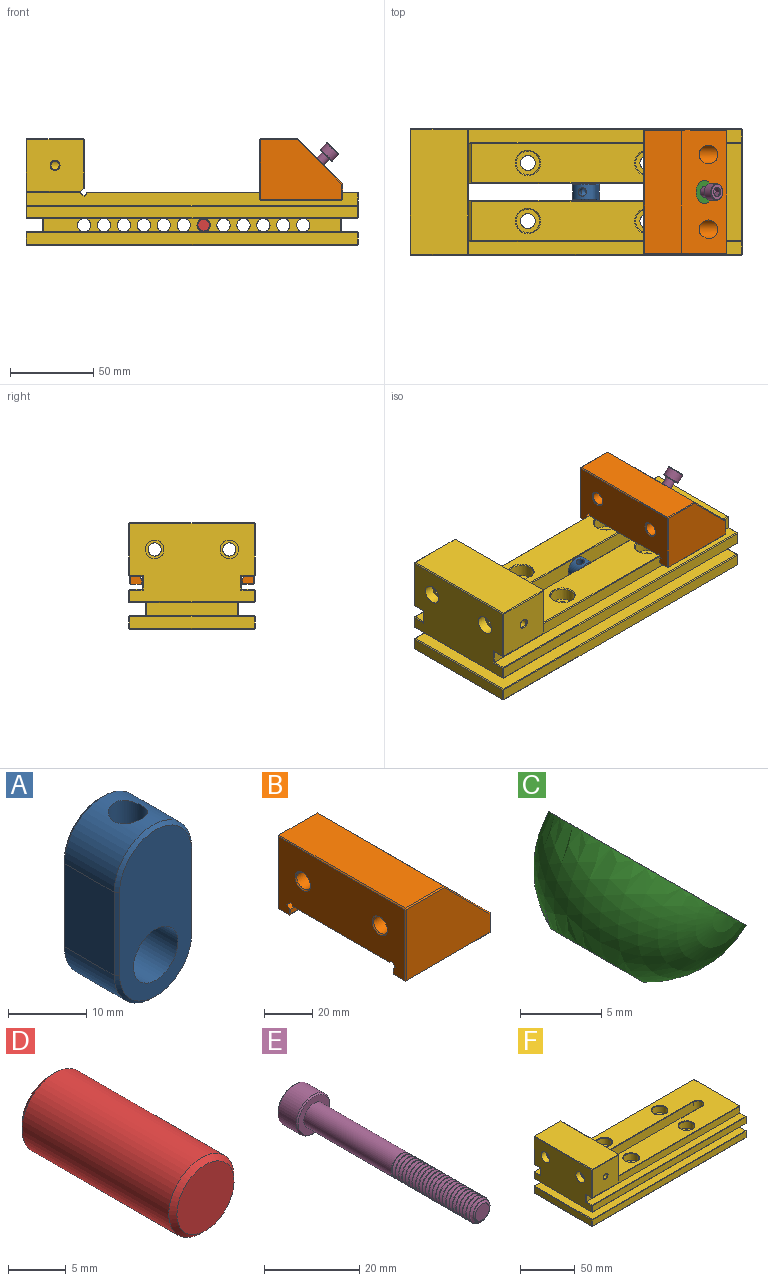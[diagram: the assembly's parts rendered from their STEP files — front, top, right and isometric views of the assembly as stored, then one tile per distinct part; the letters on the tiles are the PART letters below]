
ASSEMBLY  parts=6 mates=6
PART A: 17 faces, bbox 14x10x27 mm
  f0: cylinder r=7mm len=14mm, axis (0,1,0), area 178mm2, adj f1,f3,f7,f11,f15
  f1: plane 13x9mm, normal (-1,0,0), area 117mm2, adj f0,f2,f8,f12
  f2: cylinder r=7mm len=14mm, axis (0,1,0), area 197.9mm2, adj f1,f3,f10,f14
  f3: plane 13x9mm, normal (1,0,0), area 117mm2, adj f0,f2,f9,f13
  f4: cylinder r=4mm len=10mm, axis (0,1,0), area 251.3mm2, adj f5,f6
  f5: plane 26x13mm, normal (0,-1,0), area 251.5mm2, adj f4,f11,f12,f13,f14
  f6: plane 26x13mm, normal (0,1,0), area 251.5mm2, adj f4,f7,f8,f9,f10
  f7: cone r=7mm half-angle=45deg, axis (0,-1,0), area 15mm2, adj f0,f6,f8,f9
  f8: plane 13x0.5mm, normal (-0.71,0.71,0), area 9.2mm2, adj f1,f6,f7,f10
  f9: plane 13x0.5mm, normal (0.71,0.71,0), area 9.2mm2, adj f3,f6,f7,f10
  f10: cone r=7mm half-angle=45deg, axis (0,-1,0), area 15mm2, adj f2,f6,f8,f9
  f11: cone r=6.5mm half-angle=45deg, axis (0,1,0), area 15mm2, adj f0,f5,f12,f13
  f12: plane 13x0.5mm, normal (-0.71,-0.71,0), area 9.2mm2, adj f1,f5,f11,f14
  f13: plane 13x0.5mm, normal (0.71,-0.71,0), area 9.2mm2, adj f3,f5,f11,f14
  f14: cone r=6.5mm half-angle=45deg, axis (0,1,0), area 15mm2, adj f2,f5,f12,f13
  f15: cylinder r=2.5mm len=10.46mm, axis (0,0,1), area 160.7mm2, adj f0,f16
  f16: cone r=0mm half-angle=59deg, axis (0,0,1), area 22.9mm2, adj f15
PART B: 55 faces, bbox 50x75x42 mm
  f0: plane 55.76x49mm, normal (0,0,-1), area 2514.4mm2, adj f18,f23,f24,f51,f54
  f1: plane 74x9.5mm, normal (1,0,0), area 394.4mm2, adj f8,f9,f10,f21,f22,f23,f24,f25
  f2: plane 74x36.5mm, normal (-1,0,0), area 2228.8mm2, adj f3,f21,f22,f23,f24,f25,f26,f27
  f3: plane 49.5x6.5mm, normal (0,0,-1), area 321.7mm2, adj f2,f28,f29,f32
  f4: plane 49x36mm, normal (0,1,0), area 1407.4mm2, adj f31,f32,f33,f34,f35
  f5: plane 74x22.5mm, normal (0,0,1), area 1665mm2, adj f10,f35,f37,f38
  f6: plane 49x36mm, normal (0,-1,0), area 1407.4mm2, adj f38,f39,f41,f42,f43
  f7: plane 49x6.5mm, normal (0,0,-1), area 318.5mm2, adj f43,f46,f47,f48
  f8: plane 49.5x2.38mm, normal (0,1,0), area 117.7mm2, adj f1,f26,f48,f50
  f9: plane 49.5x2.38mm, normal (0,-1,0), area 117.7mm2, adj f1,f21,f27,f28
  f10: plane 74x27mm, normal (0.71,0,0.71), area 2390.5mm2, adj f1,f5,f11,f13,f16,f33,f39
  f11: cylinder r=5.62mm len=11.63mm, axis (1,0,0), area 212.1mm2, adj f10,f12
  f12: plane 11.25x11.25mm, normal (1,0,0), area 49.1mm2, adj f11,f19
  f13: cylinder r=5.62mm len=11.63mm, axis (1,0,0), area 212.1mm2, adj f10,f14
  f14: plane 11.25x11.25mm, normal (1,0,0), area 49.1mm2, adj f13,f20
  f15: cylinder r=4mm len=10.08mm, axis (0.71,0,0.71), area 157.2mm2, adj f16,f17
  f16: sphere r=7mm, area 252.7mm2, adj f10,f15
  f17: plane 14x9.9mm, normal (-0.71,0,-0.71), area 103.7mm2, adj f15,f18
  f18: cylinder r=7mm len=24.93mm, axis (0.71,0,0.71), area 622.9mm2, adj f0,f17
  f19: cylinder r=4mm len=32.5mm, axis (-1,0,0), area 816.8mm2, adj f12,f53
  f20: cylinder r=4mm len=32.5mm, axis (-1,0,0), area 816.8mm2, adj f14,f52
  f21: plane 50x1.77mm, normal (0,-0.71,0.71), area 124.8mm2, adj f1,f2,f9,f22,f27
  f22: plane 50x2.12mm, normal (0,-0.71,-0.71), area 150mm2, adj f1,f2,f21,f23
  f23: plane 50x1.77mm, normal (0,0.71,-0.71), area 124.6mm2, adj f0,f1,f2,f22,f51,f54
  f24: plane 50x1.77mm, normal (0,-0.71,-0.71), area 124.6mm2, adj f0,f1,f2,f25,f51,f54
  f25: plane 50x2.12mm, normal (0,0.71,-0.71), area 150mm2, adj f1,f2,f24,f26
  f26: plane 50x1.77mm, normal (0,0.71,0.71), area 124.8mm2, adj f1,f2,f8,f25,f50
  f27: plane 3.38x0.5mm, normal (-0.71,-0.71,0), area 2mm2, adj f2,f9,f21,f28
  f28: plane 50x0.5mm, normal (0,-0.71,-0.71), area 35mm2, adj f3,f9,f27,f29
  f29: plane 7x0.5mm, normal (0.71,0,-0.71), area 4.8mm2, adj f1,f3,f28,f30
  f30: plane 0.5x0.5mm, normal (0.58,0.58,-0.58), area 0.2mm2, adj f29,f31,f32
  f31: plane 9.5x0.5mm, normal (0.71,0.71,0), area 6.6mm2, adj f1,f4,f30,f33
  f32: plane 49.5x0.5mm, normal (0,0.71,-0.71), area 34.8mm2, adj f3,f4,f30,f34
  f33: plane 27.21x27.21mm, normal (0.5,0.71,0.5), area 26.9mm2, adj f4,f10,f31,f35
  f34: plane 36.5x0.5mm, normal (-0.71,0.71,0), area 25.6mm2, adj f2,f4,f32,f36
  f35: plane 22.5x0.5mm, normal (0,0.71,0.71), area 15.8mm2, adj f4,f5,f33,f36
  f36: plane 0.5x0.5mm, normal (-0.58,0.58,0.58), area 0.2mm2, adj f34,f35,f37
  f37: plane 74x0.5mm, normal (-0.71,0,0.71), area 52.3mm2, adj f2,f5,f36,f40
  f38: plane 22.5x0.5mm, normal (0,-0.71,0.71), area 15.8mm2, adj f5,f6,f39,f40
  f39: plane 27.21x27.21mm, normal (0.5,-0.71,0.5), area 26.9mm2, adj f6,f10,f38,f41
  f40: plane 0.5x0.5mm, normal (-0.58,-0.58,0.58), area 0.2mm2, adj f37,f38,f42
  f41: plane 9.5x0.5mm, normal (0.71,-0.71,0), area 6.6mm2, adj f1,f6,f39,f44
  f42: plane 36x0.5mm, normal (-0.71,-0.71,0), area 25.5mm2, adj f2,f6,f40,f45
  f43: plane 49x0.5mm, normal (0,-0.71,-0.71), area 34.6mm2, adj f6,f7,f44,f45
  f44: plane 0.5x0.5mm, normal (0.58,-0.58,-0.58), area 0.2mm2, adj f41,f43,f46
  f45: plane 0.5x0.5mm, normal (-0.58,-0.58,-0.58), area 0.2mm2, adj f42,f43,f47
  f46: plane 7x0.5mm, normal (0.71,0,-0.71), area 4.8mm2, adj f1,f7,f44,f48
  f47: plane 6.5x0.5mm, normal (-0.71,0,-0.71), area 4.6mm2, adj f2,f7,f45,f49
  f48: plane 49.5x0.5mm, normal (0,0.71,-0.71), area 34.8mm2, adj f7,f8,f46,f49
  f49: plane 0.5x0.5mm, normal (-0.58,0.58,-0.58), area 0.2mm2, adj f47,f48,f50
  f50: plane 2.88x0.5mm, normal (-0.71,0.71,0), area 1.9mm2, adj f2,f8,f26,f49
  f51: plane 56.76x0.5mm, normal (0.71,0,-0.71), area 39.8mm2, adj f0,f1,f23,f24
  f52: cone r=4mm half-angle=45deg, axis (-1,0,0), area 18.9mm2, adj f2,f20
  f53: cone r=4mm half-angle=45deg, axis (-1,0,0), area 18.9mm2, adj f2,f19
  f54: plane 56.76x0.5mm, normal (-0.71,0,-0.71), area 39.8mm2, adj f0,f2,f23,f24
PART C: 3 faces, bbox 11.9x14x11.9 mm
  f0: sphere r=7mm, area 271.5mm2, adj f1,f2
  f1: plane 14x9.9mm, normal (0.71,0,0.71), area 119.7mm2, adj f0,f2
  f2: cylinder r=3.3mm len=9.03mm, axis (0.71,0,0.71), area 128mm2, adj f0,f1
PART D: 5 faces, bbox 8x19x8 mm
  f0: plane 7x7mm, normal (0,-1,0), area 38.5mm2, adj f4
  f1: cylinder r=4mm len=18mm, axis (0,-1,0), area 452.4mm2, adj f3,f4
  f2: plane 7x7mm, normal (0,1,0), area 38.5mm2, adj f3
  f3: cone r=4mm half-angle=45deg, axis (0,-1,0), area 16.7mm2, adj f1,f2
  f4: cone r=3.5mm half-angle=45deg, axis (0,1,0), area 16.7mm2, adj f0,f1
PART E: 49 faces, bbox 11.1x57.3x11.1 mm
  f0: bspline ~24.71x6.93mm, area 299mm2, adj f2,f3,f4,f5,f6,f7,f8,f9
  f1: bspline ~24.38x6.93mm, area 298.1mm2, adj f2,f3,f4,f5,f6,f7,f8,f9
  f2: cylinder r=2.35mm len=23.82mm, axis (0,1,0), area 97.4mm2, adj f0,f1,f27,f30
  f3: cylinder r=3mm len=26.88mm, axis (0,-1,0), area 490mm2, adj f0,f1,f4,f29,f33
  f4: cylinder r=3mm len=6mm, axis (0,-1,0), area 2.4mm2, adj f0,f1,f3,f5
  f5: cylinder r=3mm len=6mm, axis (0,-1,0), area 2.4mm2, adj f0,f1,f4,f6
  f6: cylinder r=3mm len=6mm, axis (0,-1,0), area 2.4mm2, adj f0,f1,f5,f7
  f7: cylinder r=3mm len=6mm, axis (0,-1,0), area 2.4mm2, adj f0,f1,f6,f8
  f8: cylinder r=3mm len=6mm, axis (0,-1,0), area 2.4mm2, adj f0,f1,f7,f9
  f9: cylinder r=3mm len=6mm, axis (0,-1,0), area 2.4mm2, adj f0,f1,f8,f10
  f10: cylinder r=3mm len=6mm, axis (0,-1,0), area 2.4mm2, adj f0,f1,f9,f11
  f11: cylinder r=3mm len=6mm, axis (0,-1,0), area 2.4mm2, adj f0,f1,f10,f12
  f12: cylinder r=3mm len=6mm, axis (0,-1,0), area 2.4mm2, adj f0,f1,f11,f13
  f13: cylinder r=3mm len=6mm, axis (0,-1,0), area 2.4mm2, adj f0,f1,f12,f14
  f14: cylinder r=3mm len=6mm, axis (0,-1,0), area 2.4mm2, adj f0,f1,f13,f15
  f15: cylinder r=3mm len=6mm, axis (0,-1,0), area 2.4mm2, adj f0,f1,f14,f16
  f16: cylinder r=3mm len=6mm, axis (0,-1,0), area 2.4mm2, adj f0,f1,f15,f17
  f17: cylinder r=3mm len=6mm, axis (0,-1,0), area 2.4mm2, adj f0,f1,f16,f18
  f18: cylinder r=3mm len=6mm, axis (0,-1,0), area 2.4mm2, adj f0,f1,f17,f19
  f19: cylinder r=3mm len=6mm, axis (0,-1,0), area 2.4mm2, adj f0,f1,f18,f20
  f20: cylinder r=3mm len=6mm, axis (0,-1,0), area 2.4mm2, adj f0,f1,f19,f21
  f21: cylinder r=3mm len=6mm, axis (0,-1,0), area 2.4mm2, adj f0,f1,f20,f22
  f22: cylinder r=3mm len=6mm, axis (0,-1,0), area 2.4mm2, adj f0,f1,f21,f23
  f23: cylinder r=3mm len=6mm, axis (0,-1,0), area 2.4mm2, adj f0,f1,f22,f24
  f24: cylinder r=3mm len=6mm, axis (0,-1,0), area 2.4mm2, adj f0,f1,f23,f25
  f25: cylinder r=3mm len=6mm, axis (0,-1,0), area 2.4mm2, adj f0,f1,f24,f26
  f26: cylinder r=3mm len=6mm, axis (0,-1,0), area 1.3mm2, adj f0,f1,f25,f27
  f27: cone r=2.1mm half-angle=55deg, axis (0,1,0), area 10.8mm2, adj f0,f1,f2,f26,f28
  f28: plane 4.19x4.19mm, normal (0,-1,0), area 13.8mm2, adj f27
  f29: cone r=3mm half-angle=70deg, axis (0,1,0), area 4.3mm2, adj f0,f1,f3,f30
  f30: plane 5.26x3.76mm, normal (0,-1,0), area 1.6mm2, adj f0,f1,f2,f29
  f31: cylinder r=5mm len=10mm, axis (0,-1,0), area 169.6mm2, adj f47,f48
  f32: plane 10.34x10.34mm, normal (0,1,0), area 43.2mm2, adj f34,f35,f36,f37,f38,f39,f47
  f33: plane 9.4x9.4mm, normal (0,-1,0), area 41.1mm2, adj f3,f48
  f34: cone r=2.89mm half-angle=45deg, axis (0,1,0), area 0mm2, adj f32,f41
  f35: cone r=2.89mm half-angle=45deg, axis (0,1,0), area 0mm2, adj f32,f42
  f36: cone r=2.89mm half-angle=45deg, axis (0,1,0), area 0mm2, adj f32,f43
  f37: cone r=2.89mm half-angle=45deg, axis (0,1,0), area 0mm2, adj f32,f44
  f38: cone r=2.89mm half-angle=45deg, axis (0,1,0), area 0mm2, adj f32,f45
  f39: cone r=2.89mm half-angle=45deg, axis (0,1,0), area 0mm2, adj f32,f46
  f40: plane 5.77x5mm, normal (0,1,0), area 21.7mm2, adj f41,f42,f43,f44,f45,f46
  f41: plane 4.84x3.59mm, normal (-0.5,0,-0.87), area 10.1mm2, adj f34,f40,f42,f46
  f42: plane 4.85x3.99mm, normal (-1,0,0), area 10.1mm2, adj f35,f40,f41,f43
  f43: plane 4.84x3.59mm, normal (-0.5,0,0.87), area 10.1mm2, adj f36,f40,f42,f44
  f44: plane 4.84x3.59mm, normal (0.5,0,0.87), area 10.1mm2, adj f37,f40,f43,f45
  f45: plane 4.85x3.99mm, normal (1,0,0), area 10.1mm2, adj f38,f40,f44,f46
  f46: plane 4.84x3.59mm, normal (0.5,0,-0.87), area 10.1mm2, adj f39,f40,f41,f45
  f47: cone r=4.7mm half-angle=45deg, axis (0,-1,0), area 12.9mm2, adj f31,f32
  f48: cone r=5mm half-angle=45deg, axis (0,1,0), area 12.9mm2, adj f31,f33
PART F: 224 faces, bbox 200x76x64 mm
  f0: cylinder r=2.5mm len=11.88mm, axis (0,-1,0), area 179.5mm2, adj f133,f223
  f1: cylinder r=2.5mm len=12.38mm, axis (0,1,0), area 187.3mm2, adj f14,f130
  f2: cylinder r=4mm len=10.44mm, axis (0,-1,0), area 166mm2, adj f48,f52,f65,f84,f127
  f3: cylinder r=4mm len=8.44mm, axis (0,-1,0), area 178.5mm2, adj f50,f54,f127
  f4: cylinder r=4mm len=10.44mm, axis (0,-1,0), area 166mm2, adj f24,f28,f65,f84,f124
  f5: cylinder r=4mm len=8.44mm, axis (0,-1,0), area 178.5mm2, adj f26,f30,f124
  f6: cylinder r=4mm len=8.44mm, axis (0,-1,0), area 178.6mm2, adj f25,f29,f121
  f7: cylinder r=4mm len=10.44mm, axis (0,-1,0), area 166mm2, adj f23,f27,f66,f82,f121
  f8: cylinder r=4mm len=8.44mm, axis (0,-1,0), area 178.6mm2, adj f49,f53,f118
  f9: cylinder r=4mm len=10.44mm, axis (0,-1,0), area 166mm2, adj f47,f51,f66,f82,f118
  f10: plane 24.5x8mm, normal (0,1,0), area 170.9mm2, adj f78,f79,f86,f222
  f11: plane 75x47mm, normal (-1,0,0), area 3182.2mm2, adj f132,f135,f174,f178,f181,f182,f185,f187
  f12: plane 24.5x8mm, normal (0,-1,0), area 170.9mm2, adj f78,f79,f85,f139
  f13: plane 75x15mm, normal (1,0,0), area 997mm2, adj f196,f201,f202,f211,f212,f215,f218,f219
  f14: plane 34x31mm, normal (0,1,0), area 1032.7mm2, adj f1,f179,f180,f183,f186,f187
  f15: plane 162.38x59mm, normal (0,0,1), area 7285.5mm2, adj f111,f112,f136,f137,f138,f164,f165,f166
  f16: plane 34x31mm, normal (0,-1,0), area 1024.1mm2, adj f168,f169,f171,f173,f174,f223
  f17: plane 22.5x8mm, normal (0,-1,0), area 154.9mm2, adj f78,f79,f103,f220
  f18: plane 20x14mm, normal (0,0,-1), area 157.8mm2, adj f65,f66,f67,f82,f83,f84,f103,f104
  f19: plane 5x4mm, normal (0,0,-1), area 20mm2, adj f66,f82,f102,f104
  f20: plane 5x4mm, normal (0,0,-1), area 20mm2, adj f65,f84,f101,f103
  f21: plane 12x8mm, normal (0,1,0), area 45.7mm2, adj f78,f79,f102,f104
  f22: plane 12x8mm, normal (0,-1,0), area 45.7mm2, adj f78,f79,f101,f103
  f23: plane 5x4mm, normal (0,0,-1), area 20mm2, adj f7,f66,f82,f102
  f24: plane 5x4mm, normal (0,0,-1), area 20mm2, adj f4,f65,f84,f101
  f25: plane 12x8mm, normal (0,1,0), area 45.7mm2, adj f6,f78,f79,f102
  f26: plane 12x8mm, normal (0,-1,0), area 45.7mm2, adj f5,f78,f79,f101
  f27: plane 5x4mm, normal (0,0,-1), area 20mm2, adj f7,f66,f82,f100
  f28: plane 5x4mm, normal (0,0,-1), area 20mm2, adj f4,f65,f84,f99
  f29: plane 12x8mm, normal (0,1,0), area 45.7mm2, adj f6,f78,f79,f100
  f30: plane 12x8mm, normal (0,-1,0), area 45.7mm2, adj f5,f78,f79,f99
  f31: plane 5x4mm, normal (0,0,-1), area 20mm2, adj f66,f82,f98,f100
  f32: plane 5x4mm, normal (0,0,-1), area 20mm2, adj f65,f84,f97,f99
  f33: plane 12x8mm, normal (0,1,0), area 45.7mm2, adj f78,f79,f98,f100
  f34: plane 12x8mm, normal (0,-1,0), area 45.7mm2, adj f78,f79,f97,f99
  f35: plane 5x4mm, normal (0,0,-1), area 20mm2, adj f66,f82,f96,f98
  f36: plane 5x4mm, normal (0,0,-1), area 20mm2, adj f65,f84,f95,f97
  f37: plane 12x8mm, normal (0,1,0), area 45.7mm2, adj f78,f79,f96,f98
  f38: plane 12x8mm, normal (0,-1,0), area 45.7mm2, adj f78,f79,f95,f97
  f39: plane 5x4mm, normal (0,0,-1), area 20mm2, adj f66,f82,f94,f96
  f40: plane 5x4mm, normal (0,0,-1), area 20mm2, adj f65,f84,f93,f95
  f41: plane 12x8mm, normal (0,1,0), area 45.7mm2, adj f78,f79,f94,f96
  f42: plane 12x8mm, normal (0,-1,0), area 45.7mm2, adj f78,f79,f93,f95
  f43: plane 5x4mm, normal (0,0,-1), area 20mm2, adj f66,f82,f92,f94
  f44: plane 5x4mm, normal (0,0,-1), area 20mm2, adj f65,f84,f91,f93
  f45: plane 12x8mm, normal (0,1,0), area 45.7mm2, adj f78,f79,f92,f94
  f46: plane 12x8mm, normal (0,-1,0), area 45.7mm2, adj f78,f79,f91,f93
  f47: plane 5x4mm, normal (0,0,-1), area 20mm2, adj f9,f66,f82,f92
  f48: plane 5x4mm, normal (0,0,-1), area 20mm2, adj f2,f65,f84,f91
  f49: plane 12x8mm, normal (0,1,0), area 45.7mm2, adj f8,f78,f79,f92
  f50: plane 12x8mm, normal (0,-1,0), area 45.7mm2, adj f3,f78,f79,f91
  f51: plane 5x4mm, normal (0,0,-1), area 20mm2, adj f9,f66,f82,f90
  f52: plane 5x4mm, normal (0,0,-1), area 20mm2, adj f2,f65,f84,f89
  f53: plane 12x8mm, normal (0,1,0), area 45.7mm2, adj f8,f78,f79,f90
  f54: plane 12x8mm, normal (0,-1,0), area 45.7mm2, adj f3,f78,f79,f89
  f55: plane 5x4mm, normal (0,0,-1), area 20mm2, adj f66,f82,f88,f90
  f56: plane 5x4mm, normal (0,0,-1), area 20mm2, adj f65,f84,f87,f89
  f57: plane 12x8mm, normal (0,1,0), area 45.7mm2, adj f78,f79,f88,f90
  f58: plane 12x8mm, normal (0,-1,0), area 45.7mm2, adj f78,f79,f87,f89
  f59: plane 5x4mm, normal (0,0,-1), area 20mm2, adj f66,f82,f86,f88
  f60: plane 5x4mm, normal (0,0,-1), area 20mm2, adj f65,f84,f85,f87
  f61: plane 12x8mm, normal (0,1,0), area 45.7mm2, adj f78,f79,f86,f88
  f62: plane 12x8mm, normal (0,-1,0), area 45.7mm2, adj f78,f79,f85,f87
  f63: plane 20x16mm, normal (0,0,-1), area 177.8mm2, adj f64,f65,f66,f81,f82,f84,f85,f86
  f64: cylinder r=5mm len=20mm, axis (0,0,-1), area 314.2mm2, adj f63,f65,f66,f80
  f65: plane 150x20mm, normal (0,1,0), area 2624.8mm2, adj f2,f4,f18,f20,f24,f28,f32,f36
  f66: plane 150x20mm, normal (0,-1,0), area 2624.8mm2, adj f7,f9,f18,f19,f23,f27,f31,f35
  f67: cylinder r=5mm len=19.5mm, axis (0,0,-1), area 306.3mm2, adj f18,f65,f66,f138
  f68: plane 199x7mm, normal (0,-1,0), area 1393mm2, adj f190,f191,f200,f201
  f69: plane 199x7.5mm, normal (0,1,0), area 1492.5mm2, adj f79,f206,f214,f215
  f70: plane 75x7mm, normal (1,0,0), area 525mm2, adj f148,f153,f156,f159
  f71: plane 75x7mm, normal (-1,0,0), area 525mm2, adj f140,f144,f145,f146
  f72: plane 199x75mm, normal (0,0,-1), area 11296.7mm2, adj f81,f82,f83,f84,f146,f147,f155,f156
  f73: plane 75x29.38mm, normal (1,0,0), area 2102.9mm2, adj f115,f130,f133,f168,f172,f179
  f74: plane 75x34mm, normal (0,0,1), area 2550mm2, adj f172,f173,f180,f181
  f75: plane 199x7mm, normal (0,-1,0), area 1393mm2, adj f140,f143,f147,f148
  f76: plane 199x7mm, normal (0,1,0), area 1393mm2, adj f145,f154,f155,f159
  f77: plane 22.5x8mm, normal (0,1,0), area 154.9mm2, adj f78,f79,f104,f221
  f78: plane 199x75mm, normal (0,0,1), area 4845.5mm2, adj f10,f12,f17,f21,f22,f25,f26,f29
  f79: plane 199x75.5mm, normal (0,0,-1), area 4945mm2, adj f10,f12,f17,f21,f22,f25,f26,f29
  f80: plane 12.88x10mm, normal (0,0,-1), area 118.1mm2, adj f64,f65,f66,f115
  f81: cylinder r=10mm len=20mm, axis (0,0,-1), area 377mm2, adj f63,f72,f82,f84
  f82: plane 150x12mm, normal (0,-1,0), area 1498.4mm2, adj f7,f9,f18,f19,f23,f27,f31,f35
  f83: cylinder r=10mm len=20mm, axis (0,0,-1), area 377mm2, adj f18,f72,f82,f84
  f84: plane 150x12mm, normal (0,1,0), area 1498.4mm2, adj f2,f4,f18,f20,f24,f28,f32,f36
  f85: cylinder r=4mm len=23mm, axis (0,-1,0), area 515.2mm2, adj f12,f60,f62,f63,f65,f84
  f86: cylinder r=4mm len=23mm, axis (0,-1,0), area 515.2mm2, adj f10,f59,f61,f63,f66,f82
  f87: cylinder r=4mm len=23mm, axis (0,-1,0), area 515.2mm2, adj f56,f58,f60,f62,f65,f84
  f88: cylinder r=4mm len=23mm, axis (0,-1,0), area 515.2mm2, adj f55,f57,f59,f61,f66,f82
  f89: cylinder r=4mm len=23mm, axis (0,-1,0), area 515.2mm2, adj f52,f54,f56,f58,f65,f84
  f90: cylinder r=4mm len=23mm, axis (0,-1,0), area 515.2mm2, adj f51,f53,f55,f57,f66,f82
  f91: cylinder r=4mm len=23mm, axis (0,-1,0), area 515.2mm2, adj f44,f46,f48,f50,f65,f84
  f92: cylinder r=4mm len=23mm, axis (0,-1,0), area 515.2mm2, adj f43,f45,f47,f49,f66,f82
  f93: cylinder r=4mm len=23mm, axis (0,-1,0), area 515.2mm2, adj f40,f42,f44,f46,f65,f84
  f94: cylinder r=4mm len=23mm, axis (0,-1,0), area 515.2mm2, adj f39,f41,f43,f45,f66,f82
  f95: cylinder r=4mm len=23mm, axis (0,-1,0), area 515.2mm2, adj f36,f38,f40,f42,f65,f84
  f96: cylinder r=4mm len=23mm, axis (0,-1,0), area 515.2mm2, adj f35,f37,f39,f41,f66,f82
  f97: cylinder r=4mm len=23mm, axis (0,-1,0), area 515.2mm2, adj f32,f34,f36,f38,f65,f84
  f98: cylinder r=4mm len=23mm, axis (0,-1,0), area 515.2mm2, adj f31,f33,f35,f37,f66,f82
  f99: cylinder r=4mm len=23mm, axis (0,-1,0), area 515.2mm2, adj f28,f30,f32,f34,f65,f84
  f100: cylinder r=4mm len=23mm, axis (0,-1,0), area 515.2mm2, adj f27,f29,f31,f33,f66,f82
  f101: cylinder r=4mm len=23mm, axis (0,-1,0), area 515.2mm2, adj f20,f22,f24,f26,f65,f84
  f102: cylinder r=4mm len=23mm, axis (0,-1,0), area 515.2mm2, adj f19,f21,f23,f25,f66,f82
  f103: cylinder r=4mm len=23mm, axis (0,-1,0), area 515.2mm2, adj f17,f18,f20,f22,f65,f84
  f104: cylinder r=4mm len=23mm, axis (0,-1,0), area 515.2mm2, adj f18,f19,f21,f66,f77,f82
  f105: plane 32.38x8mm, normal (0,0,-1), area 243mm2, adj f106,f115,f186,f193,f204
  f106: plane 199x8mm, normal (0,1,0), area 1503mm2, adj f105,f107,f198,f204,f209,f213,f218
  f107: plane 199x7.5mm, normal (0,0,1), area 1492.5mm2, adj f106,f205,f214,f219
  f108: plane 199x7.5mm, normal (0,0,1), area 1492.5mm2, adj f109,f185,f191,f196
  f109: plane 199x8mm, normal (0,-1,0), area 1503mm2, adj f108,f110,f182,f192,f197,f202,f203
  f110: plane 32.38x8mm, normal (0,0,-1), area 243mm2, adj f109,f115,f171,f178,f192
  f111: plane 24.5x2.12mm, normal (-0.71,0,0.71), area 73.3mm2, adj f15,f66,f113,f136,f209
  f112: plane 24.5x2.12mm, normal (-0.71,0,0.71), area 73.3mm2, adj f15,f65,f114,f137,f197
  f113: plane 24.5x2.12mm, normal (0.71,0,0.71), area 73.5mm2, adj f66,f111,f115,f204
  f114: plane 24.5x2.12mm, normal (0.71,0,0.71), area 73.5mm2, adj f65,f112,f115,f192
  f115: plane 75x2.12mm, normal (0.71,0,-0.71), area 225mm2, adj f73,f80,f105,f110,f113,f114,f169,f183
  f116: plane 55x8mm, normal (1,0,0), area 440mm2, adj f78,f79,f220,f221
  f117: plane 55x8mm, normal (-1,0,0), area 440mm2, adj f78,f79,f139,f222
  f118: cylinder r=4.5mm len=23.5mm, axis (0,0,1), area 548.5mm2, adj f8,f9,f119,f161
  f119: plane 14.25x14.25mm, normal (0,0,1), area 95.9mm2, adj f118,f120
  f120: cylinder r=7.12mm len=14.25mm, axis (0,0,1), area 335.8mm2, adj f119,f164
  f121: cylinder r=4.5mm len=23.5mm, axis (0,0,1), area 548.5mm2, adj f6,f7,f122,f163
  f122: plane 14.25x14.25mm, normal (0,0,1), area 95.9mm2, adj f121,f123
  f123: cylinder r=7.12mm len=14.25mm, axis (0,0,1), area 335.8mm2, adj f122,f167
  f124: cylinder r=4.5mm len=23.5mm, axis (0,0,1), area 548.5mm2, adj f4,f5,f125,f162
  f125: plane 14.25x14.25mm, normal (0,0,1), area 95.9mm2, adj f124,f126
  f126: cylinder r=7.12mm len=14.25mm, axis (0,0,1), area 335.8mm2, adj f125,f166
  f127: cylinder r=4.5mm len=23.5mm, axis (0,0,1), area 548.5mm2, adj f2,f3,f128,f160
  f128: plane 14.25x14.25mm, normal (0,0,1), area 95.9mm2, adj f127,f129
  f129: cylinder r=7.12mm len=14.25mm, axis (0,0,1), area 335.8mm2, adj f128,f165
  f130: cylinder r=4mm len=29mm, axis (-1,0,0), area 708.1mm2, adj f1,f73,f131
  f131: plane 11.25x11.25mm, normal (-1,0,0), area 49.1mm2, adj f130,f132
  f132: cylinder r=5.62mm len=11.25mm, axis (-1,0,0), area 212.1mm2, adj f11,f131
  f133: cylinder r=4mm len=29mm, axis (-1,0,0), area 708mm2, adj f0,f73,f134
  f134: plane 11.25x11.25mm, normal (-1,0,0), area 49.1mm2, adj f133,f135
  f135: cylinder r=5.62mm len=11.25mm, axis (-1,0,0), area 212.1mm2, adj f11,f134
  f136: plane 138.38x0.5mm, normal (0,-0.71,0.71), area 97.7mm2, adj f15,f66,f111,f138
  f137: plane 138.38x0.5mm, normal (0,0.71,0.71), area 97.7mm2, adj f15,f65,f112,f138
  f138: cone r=5.5mm half-angle=45deg, axis (0,0,1), area 11.7mm2, adj f15,f67,f136,f137
  f139: plane 8x0.5mm, normal (-0.71,-0.71,0), area 5.7mm2, adj f12,f78,f79,f117
  f140: plane 7x0.5mm, normal (-0.71,-0.71,0), area 4.9mm2, adj f71,f75,f141,f142
  f141: plane 0.5x0.5mm, normal (-0.58,-0.58,0.58), area 0.2mm2, adj f140,f143,f144
  f142: plane 0.5x0.5mm, normal (-0.58,-0.58,-0.58), area 0.2mm2, adj f140,f146,f147
  f143: plane 199x0.5mm, normal (0,-0.71,0.71), area 140.7mm2, adj f75,f78,f141,f149
  f144: plane 75x0.5mm, normal (-0.71,0,0.71), area 53mm2, adj f71,f78,f141,f150
  f145: plane 7x0.5mm, normal (-0.71,0.71,0), area 4.9mm2, adj f71,f76,f150,f151
  f146: plane 75x0.5mm, normal (-0.71,0,-0.71), area 53mm2, adj f71,f72,f142,f151
  f147: plane 199x0.5mm, normal (0,-0.71,-0.71), area 140.7mm2, adj f72,f75,f142,f152
  f148: plane 7x0.5mm, normal (0.71,-0.71,0), area 4.9mm2, adj f70,f75,f149,f152
  f149: plane 0.5x0.5mm, normal (0.58,-0.58,0.58), area 0.2mm2, adj f143,f148,f153
  f150: plane 0.5x0.5mm, normal (-0.58,0.58,0.58), area 0.2mm2, adj f144,f145,f154
  f151: plane 0.5x0.5mm, normal (-0.58,0.58,-0.58), area 0.2mm2, adj f145,f146,f155
  f152: plane 0.5x0.5mm, normal (0.58,-0.58,-0.58), area 0.2mm2, adj f147,f148,f156
  f153: plane 75x0.5mm, normal (0.71,0,0.71), area 53mm2, adj f70,f78,f149,f157
  f154: plane 199x0.5mm, normal (0,0.71,0.71), area 140.7mm2, adj f76,f78,f150,f157
  f155: plane 199x0.5mm, normal (0,0.71,-0.71), area 140.7mm2, adj f72,f76,f151,f158
  f156: plane 75x0.5mm, normal (0.71,0,-0.71), area 53mm2, adj f70,f72,f152,f158
  f157: plane 0.5x0.5mm, normal (0.58,0.58,0.58), area 0.2mm2, adj f153,f154,f159
  f158: plane 0.5x0.5mm, normal (0.58,0.58,-0.58), area 0.2mm2, adj f155,f156,f159
  f159: plane 7x0.5mm, normal (0.71,0.71,0), area 4.9mm2, adj f70,f76,f157,f158
  f160: cone r=5mm half-angle=45deg, axis (0,0,-1), area 21.1mm2, adj f72,f127
  f161: cone r=5mm half-angle=45deg, axis (0,0,-1), area 21.1mm2, adj f72,f118
  f162: cone r=5mm half-angle=45deg, axis (0,0,-1), area 21.1mm2, adj f72,f124
  f163: cone r=5mm half-angle=45deg, axis (0,0,-1), area 21.1mm2, adj f72,f121
  f164: cone r=7.12mm half-angle=45deg, axis (0,0,1), area 32.8mm2, adj f15,f120
  f165: cone r=7.12mm half-angle=45deg, axis (0,0,1), area 32.8mm2, adj f15,f129
  f166: cone r=7.12mm half-angle=45deg, axis (0,0,1), area 32.8mm2, adj f15,f126
  f167: cone r=7.12mm half-angle=45deg, axis (0,0,1), area 32.8mm2, adj f15,f123
  f168: plane 29.38x0.5mm, normal (0.71,-0.71,0), area 20.7mm2, adj f16,f73,f169,f170
  f169: plane 2.33x2.33mm, normal (0.5,-0.71,-0.5), area 2mm2, adj f16,f115,f168,f171
  f170: plane 0.5x0.5mm, normal (0.58,-0.58,0.58), area 0.2mm2, adj f168,f172,f173
  f171: plane 32.38x0.5mm, normal (0,-0.71,-0.71), area 22.8mm2, adj f16,f110,f169,f175
  f172: plane 75x0.5mm, normal (0.71,0,0.71), area 53mm2, adj f73,f74,f170,f176
  f173: plane 34x0.5mm, normal (0,-0.71,0.71), area 24mm2, adj f16,f74,f170,f177
  f174: plane 31x0.5mm, normal (-0.71,-0.71,0), area 21.9mm2, adj f11,f16,f175,f177
  f175: plane 0.5x0.5mm, normal (-0.58,-0.58,-0.58), area 0.2mm2, adj f171,f174,f178
  f176: plane 0.5x0.5mm, normal (0.58,0.58,0.58), area 0.2mm2, adj f172,f179,f180
  f177: plane 0.5x0.5mm, normal (-0.58,-0.58,0.58), area 0.2mm2, adj f173,f174,f181
  f178: plane 8x0.5mm, normal (-0.71,0,-0.71), area 5.5mm2, adj f11,f110,f175,f182
  f179: plane 29.38x0.5mm, normal (0.71,0.71,0), area 20.7mm2, adj f14,f73,f176,f183
  f180: plane 34x0.5mm, normal (0,0.71,0.71), area 24mm2, adj f14,f74,f176,f184
  f181: plane 75x0.5mm, normal (-0.71,0,0.71), area 53mm2, adj f11,f74,f177,f184
  f182: plane 9x0.5mm, normal (-0.71,-0.71,0), area 6mm2, adj f11,f109,f178,f185
  f183: plane 2.33x2.33mm, normal (0.5,0.71,-0.5), area 2mm2, adj f14,f115,f179,f186
  f184: plane 0.5x0.5mm, normal (-0.58,0.58,0.58), area 0.2mm2, adj f180,f181,f187
  f185: plane 8x0.5mm, normal (-0.71,0,0.71), area 5.5mm2, adj f11,f108,f182,f188
  f186: plane 32.38x0.5mm, normal (0,0.71,-0.71), area 22.8mm2, adj f14,f105,f183,f189
  f187: plane 31x0.5mm, normal (-0.71,0.71,0), area 21.9mm2, adj f11,f14,f184,f189
  f188: plane 0.5x0.5mm, normal (-0.58,-0.58,0.58), area 0.2mm2, adj f185,f190,f191
  f189: plane 0.5x0.5mm, normal (-0.58,0.58,-0.58), area 0.2mm2, adj f186,f187,f193
  f190: plane 7x0.5mm, normal (-0.71,-0.71,0), area 4.9mm2, adj f11,f68,f188,f194
  f191: plane 199x0.5mm, normal (0,-0.71,0.71), area 140.7mm2, adj f68,f108,f188,f195
  f192: plane 2.83x2.83mm, normal (0.5,-0.71,0.5), area 2.5mm2, adj f109,f110,f114,f197
  f193: plane 8x0.5mm, normal (-0.71,0,-0.71), area 5.5mm2, adj f11,f105,f189,f198
  f194: plane 0.5x0.5mm, normal (-0.58,-0.58,-0.58), area 0.2mm2, adj f190,f199,f200
  f195: plane 0.5x0.5mm, normal (0.58,-0.58,0.58), area 0.2mm2, adj f191,f196,f201
  f196: plane 8x0.5mm, normal (0.71,0,0.71), area 5.5mm2, adj f13,f108,f195,f202
  f197: plane 2.83x2.33mm, normal (-0.5,-0.71,0.5), area 2.2mm2, adj f109,f112,f192,f203
  f198: plane 9x0.5mm, normal (-0.71,0.71,0), area 6mm2, adj f11,f106,f193,f205
  f199: plane 75.5x0.5mm, normal (-0.71,0,-0.71), area 53.2mm2, adj f11,f79,f194,f206
  f200: plane 199x0.5mm, normal (0,-0.71,-0.71), area 140.7mm2, adj f68,f79,f194,f207
  f201: plane 7x0.5mm, normal (0.71,-0.71,0), area 4.9mm2, adj f13,f68,f195,f207
  f202: plane 8x0.5mm, normal (0.71,-0.71,0), area 5.5mm2, adj f13,f109,f196,f208
  f203: plane 162.38x0.5mm, normal (0,-0.71,0.71), area 114.7mm2, adj f15,f109,f197,f208
  f204: plane 2.83x2.83mm, normal (0.5,0.71,0.5), area 2.5mm2, adj f105,f106,f113,f209
  f205: plane 8x0.5mm, normal (-0.71,0,0.71), area 5.5mm2, adj f11,f107,f198,f210
  f206: plane 7.5x0.5mm, normal (-0.71,0.71,0), area 5.1mm2, adj f11,f69,f199,f210
  f207: plane 0.5x0.5mm, normal (0.58,-0.58,-0.58), area 0.2mm2, adj f200,f201,f211
  f208: plane 0.5x0.5mm, normal (0.58,-0.58,0.58), area 0.2mm2, adj f202,f203,f212
  f209: plane 2.83x2.33mm, normal (-0.5,0.71,0.5), area 2.2mm2, adj f106,f111,f204,f213
  f210: plane 0.5x0.5mm, normal (-0.58,0.58,0.58), area 0.2mm2, adj f205,f206,f214
  f211: plane 75.5x0.5mm, normal (0.71,0,-0.71), area 53.2mm2, adj f13,f79,f207,f215
  f212: plane 59x0.5mm, normal (0.71,0,0.71), area 41.7mm2, adj f13,f15,f208,f216
  f213: plane 162.38x0.5mm, normal (0,0.71,0.71), area 114.7mm2, adj f15,f106,f209,f216
  f214: plane 199x0.5mm, normal (0,0.71,0.71), area 140.7mm2, adj f69,f107,f210,f217
  f215: plane 7.5x0.5mm, normal (0.71,0.71,0), area 5.1mm2, adj f13,f69,f211,f217
  f216: plane 0.5x0.5mm, normal (0.58,0.58,0.58), area 0.2mm2, adj f212,f213,f218
  f217: plane 0.5x0.5mm, normal (0.58,0.58,0.58), area 0.2mm2, adj f214,f215,f219
  f218: plane 8x0.5mm, normal (0.71,0.71,0), area 5.5mm2, adj f13,f106,f216,f219
  f219: plane 8x0.5mm, normal (0.71,0,0.71), area 5.5mm2, adj f13,f107,f217,f218
  f220: plane 8x0.5mm, normal (0.71,-0.71,0), area 5.7mm2, adj f17,f78,f79,f116
  f221: plane 8x0.5mm, normal (0.71,0.71,0), area 5.7mm2, adj f77,f78,f79,f116
  f222: plane 8x0.5mm, normal (-0.71,0.71,0), area 5.7mm2, adj f10,f78,f79,f117
  f223: cone r=2.5mm half-angle=45deg, axis (0,-1,0), area 12.2mm2, adj f0,f16
PLACE A rot(axis=(0,-1,0),9.1deg) t=(4.99,-18.49,38.11)mm
PLACE B t=(-4.96,-18.49,23.17)mm
PLACE C t=(-4.96,-18.49,23.17)mm
PLACE D rot(axis=(0,-1,0),9.1deg) t=(4.99,-18.74,38.11)mm
PLACE E rot(axis=(0.68,0.68,0.28),148.6deg) t=(-50.35,-18.49,41.79)mm
PLACE F t=(4.27,-18.49,23.17)mm fixed
MATE planar A.f0 <-> F.f65  axis (0,-1,0) through (-90.8,-23.49,48.01)mm
MATE fastened C.f2 <-> B.f18  axis (0.71,0,0.71) through (-18.46,-18.49,73.67)mm
MATE cylindrical F.f95 <-> A.f2  axis (0,1,0) through (-88.73,-23.49,35.17)mm
MATE fastened A.f2 <-> D.f1  axis (0,1,0) through (-88.73,-23.49,35.17)mm
MATE slider E.f2 <-> C.f2  axis (-0.71,0,-0.71) through (-50.35,-18.49,41.79)mm
MATE planar B.f0 <-> F.f15  axis (0,0,-1) through (-5.46,-18.49,55.17)mm
